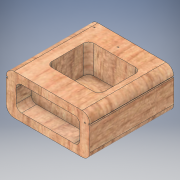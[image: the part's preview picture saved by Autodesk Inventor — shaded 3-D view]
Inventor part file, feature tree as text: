
AUTODESK INVENTOR PART (.ipt)
format: ipt  version: 2017 (Build 210142000, 142)  size: 217,088 bytes
history: native  units: in
note: dims shown in document units (in); Inventor stores cm internally (conversion verified against a paired STEP export)
features: extrude x6, sketch x6
ambient origin geometry x8: Origin, YZ Plane, XZ Plane, XY Plane, X Axis, Y Axis, Z Axis, Center Point
bodies: Solid1 (feature_tree)
feature tree (12):
  extrude  "Extrusion1"  Depth=1.53in
  extrude  "Extrusion2"  Depth=0.3in
  extrude  "Extrusion3"  Depth=0.3in
  extrude  "Extrusion4"  Depth=2.4in
  extrude  "Extrusion5"  Depth=0.2in
  extrude  "Extrusion6"  Depth=1.59in
  sketch  "Sketch1"  dims[d2=3.17in d3=1.53in]
  sketch  "Sketch2"  dims[d4=0.3in d5=0.3in]
  sketch  "Sketch3"  dims[d6=0.3in d7=0.3in]
  sketch  "Sketch4"  dims[d10=3.17in d11=0.0in d12=2.4in]
  sketch  "Sketch5"  dims[d13=0.93in d16=0.2in]
  sketch  "Sketch6"  dims[d17=0.57in d18=0.0in d19=1.59in d20=1.98in d21=0.5in d22=1.07in d23=0.0in d26=1.0in d27=2.5in d29=1.0in d30=0.2in d31=0.57in d32=0.0in d33=0.2in d34=0.06in d35=0.05in d36=0.0in d37=0.05in d38=0.0in]
